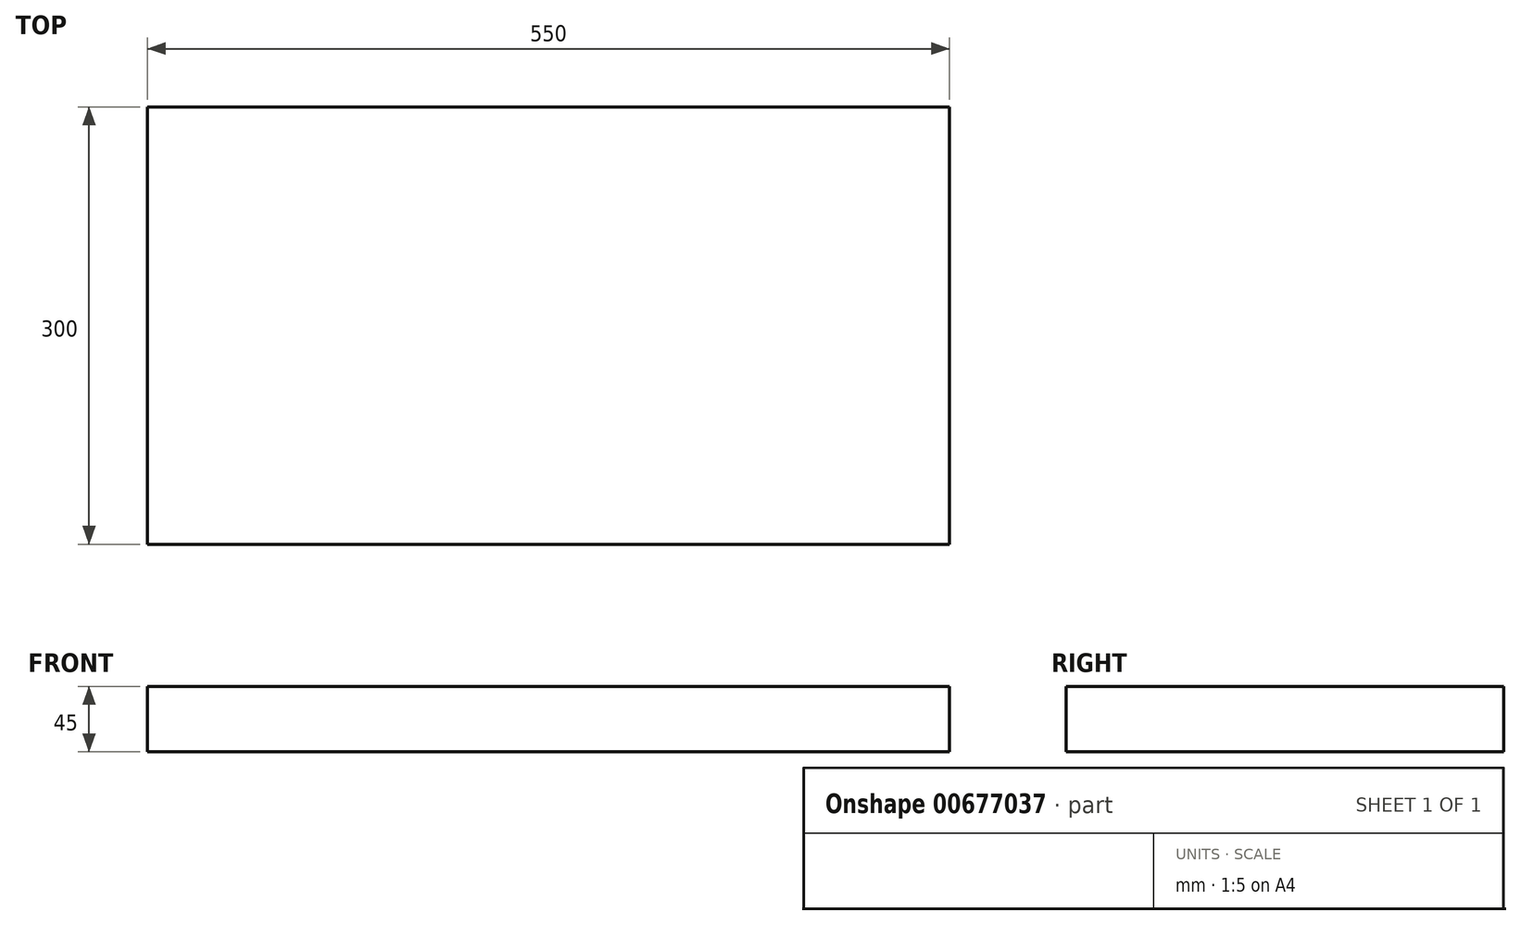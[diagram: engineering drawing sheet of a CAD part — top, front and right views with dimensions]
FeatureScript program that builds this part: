
annotation { "Feature Type Name" : "Feature", "Feature Type Description" : "" }
export const myFeature = defineFeature(function(context is Context, id is Id, definition is map)
    precondition{}
    {
        {
            var Q0;
            Q0=qCreatedBy(makeId("Top.planeOp"),FACE);
            var sketch = newSketch(context, id + "F0", { "sketchPlane" : qUnion([Q0])});
            skLineSegment(sketch, "E0.bottom", {"start": v(0, 0) * mm, "end": v(550, 0) * mm});
            skLineSegment(sketch, "E0.top", {"start": v(0, -300) * mm, "end": v(550, -300) * mm});
            skLineSegment(sketch, "E0.left", {"start": v(0, 0) * mm, "end": v(0, -300) * mm});
            skLineSegment(sketch, "E0.right", {"start": v(550, 0) * mm, "end": v(550, -300) * mm});
            skSolve(sketch);
        }
        {
            var Q0;
            Q0=makeQuery(id+"F0.imprint","IMPRINT",FACE,{"disambiguationData":[TD([[makeQuery(id+"F0.imprint","IMPRINT",EDGE,{"derivedFrom":sQuery(id+"F0.wireOp",EDGE,"E0.bottom")}),-1.0]])]});
            extrude(context, id + "F1", {"entities" : qUnion([Q0]), "depth" : 45 * mm, "offsetDistance" : 25 * mm});
        }
    });
